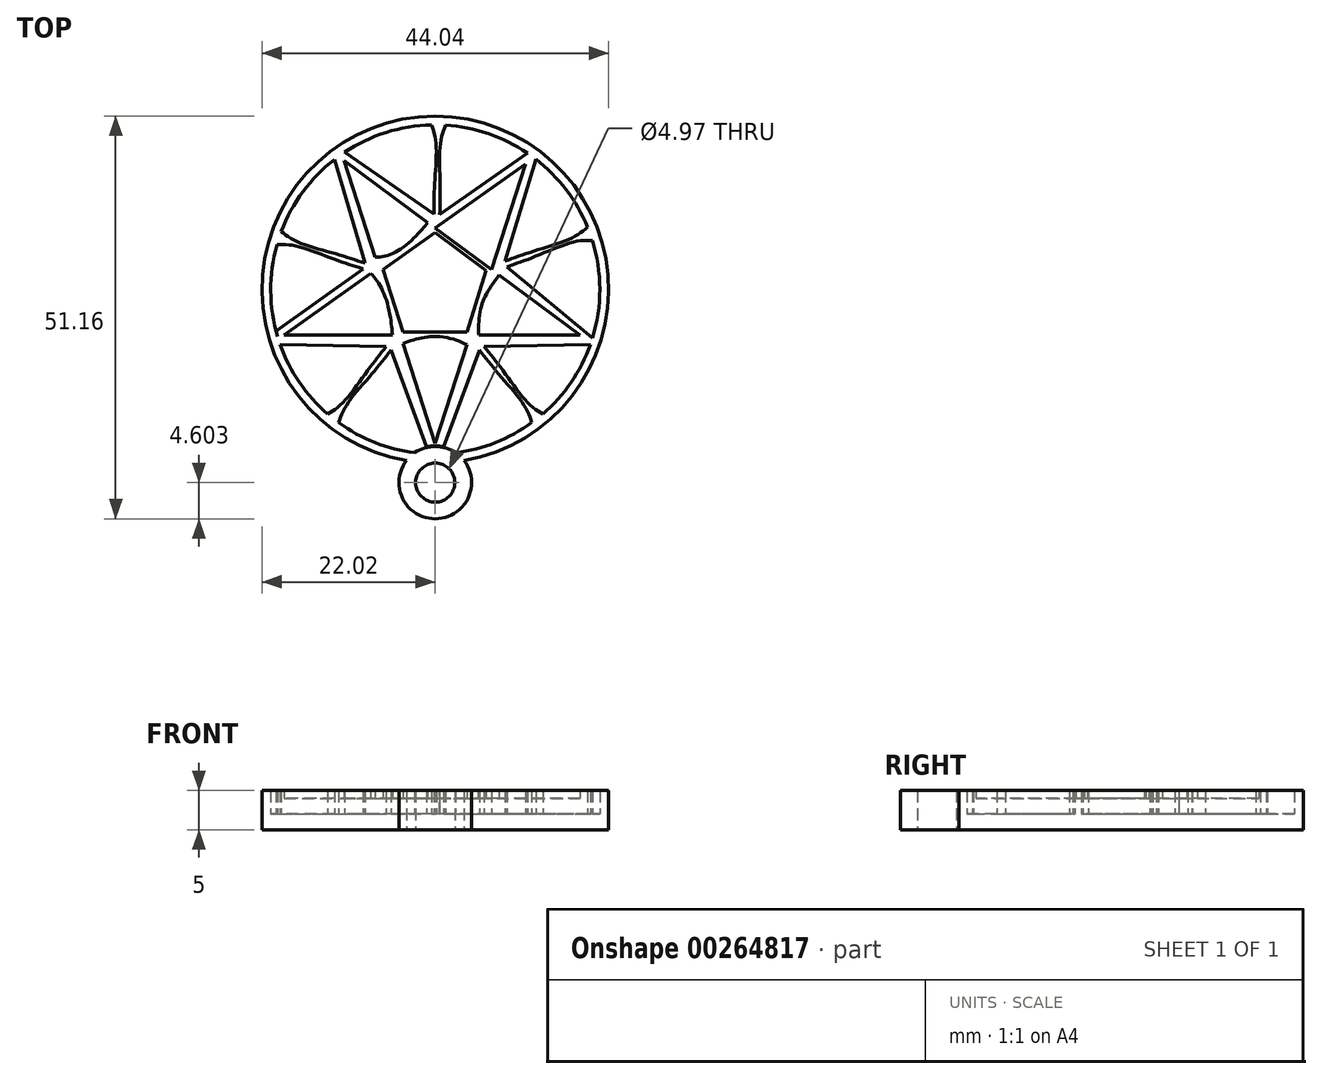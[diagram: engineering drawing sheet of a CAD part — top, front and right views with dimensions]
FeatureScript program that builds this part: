
annotation { "Feature Type Name" : "Feature", "Feature Type Description" : "" }
export const myFeature = defineFeature(function(context is Context, id is Id, definition is map)
    precondition{}
    {
        {
            var Q0;
            Q0=qCreatedBy(makeId("Top.planeOp"),FACE);
            var sketch = newSketch(context, id + "F0", { "sketchPlane" : qUnion([Q0])});
            skCircle(sketch, "E0", {"center": v(0, 0) * mm, "radius": 22.02 * mm});
            skLineSegment(sketch, "E1", {"start": v(0, 0) * mm, "end": v(0, 22.02) * mm, "construction": true});
            skLineSegment(sketch, "E2", {"start": v(0, 0) * mm, "end": v(20.72, 7.45) * mm, "construction": true});
            skLineSegment(sketch, "E3", {"start": v(0, 0) * mm, "end": v(13.06, -17.72) * mm, "construction": true});
            skLineSegment(sketch, "E4", {"start": v(0, 0) * mm, "end": v(-13.06, -17.72) * mm, "construction": true});
            skLineSegment(sketch, "E5", {"start": v(0, 0) * mm, "end": v(-20.91, 6.88) * mm, "construction": true});
            skLineSegment(sketch, "E6", {"start": v(-13.06, 17.72) * mm, "end": v(0, -22.02) * mm, "construction": true});
            skLineSegment(sketch, "E7", {"start": v(0, -22.02) * mm, "end": v(13.06, 17.72) * mm, "construction": true});
            skLineSegment(sketch, "E8", {"start": v(13.06, 17.72) * mm, "end": v(-20.91, -6.88) * mm, "construction": true});
            skLineSegment(sketch, "E9", {"start": v(-20.91, -6.88) * mm, "end": v(20.72, -6.88) * mm, "construction": true});
            skLineSegment(sketch, "E10", {"start": v(20.72, -6.88) * mm, "end": v(-13.06, 17.72) * mm, "construction": true});
            skCircle(sketch, "E11", {"center": v(0, 0) * mm, "radius": 20.9 * mm});
            skLineSegment(sketch, "E12", {"start": v(-11.47, 15.95) * mm, "end": v(0, -18.94) * mm});
            skLineSegment(sketch, "E13", {"start": v(0, -18.94) * mm, "end": v(11.36, 15.61) * mm});
            skLineSegment(sketch, "E14", {"start": v(11.36, 15.61) * mm, "end": v(-18.96, -5.83) * mm});
            skLineSegment(sketch, "E15", {"start": v(-18.96, -5.83) * mm, "end": v(18.12, -5.83) * mm});
            skLineSegment(sketch, "E16", {"start": v(18.12, -5.83) * mm, "end": v(-11.47, 15.95) * mm});
            skSolve(sketch);
        }
        {
            var Q0;
            Q0=makeQuery(id+"F0.imprint","IMPRINT",FACE,{"disambiguationData":[TD([[makeQuery(id+"F0.imprint","IMPRINT",EDGE,{"derivedFrom":sQuery(id+"F0.wireOp",EDGE,"E11")}),1.0]])]});
            var Q1;
            {var subQ0=sQuery(id+"F0.wireOp",EDGE,"E14");var subQ1=sQuery(id+"F0.wireOp",EDGE,"E13");var subQ2=makeQuery(id+"F0.imprint","INTERSECT",VERTEX,{"derivedFrom":[subQ1,subQ0]});Q1=makeQuery(id+"F0.imprint","IMPRINT",FACE,{"disambiguationData":[TD([[makeQuery(id+"F0.imprint","IMPRINT",EDGE,{"disambiguationData":[TD([[subQ2,1.0]])],"derivedFrom":subQ1}),1.0]])]});}
            var Q2;
            {var subQ0=sQuery(id+"F0.wireOp",EDGE,"E16");var subQ1=sQuery(id+"F0.wireOp",EDGE,"E12");var subQ2=makeQuery(id+"F0.imprint","INTERSECT",VERTEX,{"derivedFrom":[subQ1,subQ0]});Q2=makeQuery(id+"F0.imprint","IMPRINT",FACE,{"disambiguationData":[TD([[makeQuery(id+"F0.imprint","IMPRINT",EDGE,{"disambiguationData":[TD([[subQ2,-1.0]])],"derivedFrom":subQ1}),1.0]])]});}
            var Q3;
            {var subQ0=sQuery(id+"F0.wireOp",EDGE,"E14");var subQ1=sQuery(id+"F0.wireOp",EDGE,"E12");var subQ2=makeQuery(id+"F0.imprint","INTERSECT",VERTEX,{"derivedFrom":[subQ1,subQ0]});Q3=makeQuery(id+"F0.imprint","IMPRINT",FACE,{"disambiguationData":[TD([[makeQuery(id+"F0.imprint","IMPRINT",EDGE,{"disambiguationData":[TD([[subQ2,-1.0]])],"derivedFrom":subQ1}),-1.0]])]});}
            var Q4;
            {var subQ0=sQuery(id+"F0.wireOp",EDGE,"E13");var subQ1=sQuery(id+"F0.wireOp",EDGE,"E12");var subQ2=makeQuery(id+"F0.imprint","INTERSECT",VERTEX,{"derivedFrom":[subQ1,subQ0]});Q4=makeQuery(id+"F0.imprint","IMPRINT",FACE,{"disambiguationData":[TD([[makeQuery(id+"F0.imprint","IMPRINT",EDGE,{"disambiguationData":[TD([[subQ2,1.0]])],"derivedFrom":subQ1}),1.0]])]});}
            var Q5;
            {var subQ0=sQuery(id+"F0.wireOp",EDGE,"E15");var subQ1=sQuery(id+"F0.wireOp",EDGE,"E13");var subQ2=makeQuery(id+"F0.imprint","INTERSECT",VERTEX,{"derivedFrom":[subQ1,subQ0]});Q5=makeQuery(id+"F0.imprint","IMPRINT",FACE,{"disambiguationData":[TD([[makeQuery(id+"F0.imprint","IMPRINT",EDGE,{"disambiguationData":[TD([[subQ2,-1.0]])],"derivedFrom":subQ1}),-1.0]])]});}
            var Q6;
            {var subQ1=sQuery(id+"F0.wireOp",EDGE,"E12");var subQ5=sQuery(id+"F0.wireOp",EDGE,"E14");var subQ6=makeQuery(id+"F0.imprint","INTERSECT",VERTEX,{"derivedFrom":[subQ1,subQ5]});Q6=makeQuery(id+"F0.imprint","IMPRINT",FACE,{"disambiguationData":[TD([[makeQuery(id+"F0.imprint","IMPRINT",EDGE,{"disambiguationData":[TD([[subQ6,-1.0]])],"derivedFrom":subQ1}),1.0]])]});}
            extrude(context, id + "F1", {"entities" : qUnion([Q0, Q1, Q2, Q3, Q4, Q5, Q6]), "depth" : 2 * mm, "offsetDistance" : 25 * mm});
        }
        {
            var Q0;
            Q0=makeQuery(id+"F0.imprint","IMPRINT",FACE,{"disambiguationData":[TD([[makeQuery(id+"F0.imprint","IMPRINT",EDGE,{"derivedFrom":sQuery(id+"F0.wireOp",EDGE,"E0")}),1.0]])]});
            extrude(context, id + "F2", {"entities" : qUnion([Q0]), "operationType" : NewBodyOperationType.ADD, "depth" : 5 * mm, "offsetDistance" : 25 * mm});
        }
        {
            var Q0;
            Q0=makeQuery(id+"F1.opExtrude","CAP_FACE",FACE,{"disambiguationData":[OSD([sQuery(id+"F0.wireOp",EDGE,"E11")])],"isStart":false});
            var sketch = newSketch(context, id + "F3", { "sketchPlane" : qUnion([Q0])});
            skLineSegment(sketch, "E17", {"start": v(-11.59, 16.36) * mm, "end": v(0, -19.6) * mm});
            skLineSegment(sketch, "E18", {"start": v(0, -19.6) * mm, "end": v(11.46, 15.95) * mm});
            skLineSegment(sketch, "E19", {"start": v(11.46, 15.95) * mm, "end": v(-19.22, -5.77) * mm});
            skLineSegment(sketch, "E20", {"start": v(-19.22, -5.77) * mm, "end": v(18.4, -5.77) * mm});
            skLineSegment(sketch, "E21", {"start": v(18.4, -5.77) * mm, "end": v(-11.59, 16.36) * mm});
            skPoint(sketch, "E22.2.internal.snap0", {"position": v(-3.88, 5.1) * mm});
            skFitSpline(sketch, "E22", {"points": [v(-7.63, 4.09) * mm, v(-6, 4.35) * mm, v(-3.88, 5.51) * mm, v(-1.86, 7.4) * mm, v(-0.97, 8.52) * mm], "startDerivative": vector(7.1, 0.61) * mm, "endDerivative": vector(3.7, 5) * mm});
            skFitSpline(sketch, "E23.MirrorCS", {"points": [v(7.63, 4.09) * mm, v(6, 4.35) * mm, v(3.88, 5.51) * mm, v(1.86, 7.4) * mm, v(0.97, 8.52) * mm], "startDerivative": vector(-7.1, 0.61) * mm, "endDerivative": vector(-3.7, 5) * mm});
            skFitSpline(sketch, "E24", {"points": [v(0.97, 8.52) * mm, v(1.86, 7.4) * mm, v(3.88, 5.51) * mm, v(6, 4.35) * mm, v(7.63, 4.09) * mm], "startDerivative": vector(3.71, -5.02) * mm, "endDerivative": vector(7.1, -0.61) * mm});
            skFitSpline(sketch, "E25", {"points": [v(-8.2, 2.03) * mm, v(-7.19, 0.78) * mm, v(-6.13, -1.62) * mm, v(-5.57, -4.53) * mm, v(-5.44, -5.77) * mm], "startDerivative": vector(4.84, -5) * mm, "endDerivative": vector(0.3, -5.7) * mm});
            skPoint(sketch, "E26", {"position": v(-5.8, -1.62) * mm});
            skFitSpline(sketch, "E27", {"points": [v(-4.1, -6.89) * mm, v(-2.2, -6.27) * mm, v(0, -5.98) * mm, v(2.75, -6.44) * mm, v(4.05, -7.03) * mm], "startDerivative": vector(7.54, 3.7) * mm, "endDerivative": vector(5.89, -2.67) * mm});
            skFitSpline(sketch, "E28", {"points": [v(8.1, 1.83) * mm, v(6.5, -0.54) * mm, v(5.83, -2.25) * mm, v(5.5, -4.78) * mm, v(5.54, -5.77) * mm], "startDerivative": vector(-5.96, -8.34) * mm, "endDerivative": vector(0.52, -4.8) * mm});
            skFitSpline(sketch, "E29", {"points": [v(-20.36, 5.66) * mm, v(-17.82, 5.55) * mm, v(-12.86, 3.85) * mm, v(-9.19, 2.62) * mm], "startDerivative": vector(8.48, 0.55) * mm, "endDerivative": vector(10.23, -3.2) * mm});
            skFitSpline(sketch, "E30.MirrorCS", {"points": [v(-19.75, 7.53) * mm, v(-17.64, 6.1) * mm, v(-12.63, 4.53) * mm, v(-8.95, 3.34) * mm], "startDerivative": vector(6.5, -5.47) * mm, "endDerivative": vector(10.13, -3.49) * mm});
            skLineSegment(sketch, "E31", {"start": v(-19.22, -5.77) * mm, "end": v(0, 0) * mm, "construction": true});
            skLineSegment(sketch, "E32", {"start": v(0, 0) * mm, "end": v(11.46, 15.95) * mm, "construction": true});
            skLineSegment(sketch, "E33", {"start": v(-11.59, 16.36) * mm, "end": v(-10.84, 15.8) * mm, "construction": true});
            skLineSegment(sketch, "E34", {"start": v(-11.59, 16.36) * mm, "end": v(0, 0) * mm, "construction": true});
            skLineSegment(sketch, "E35", {"start": v(0, -0.7) * mm, "end": v(0, 0) * mm, "construction": true});
            skFitSpline(sketch, "E36.MirrorCS", {"points": [v(-13.87, -15.94) * mm, v(-11.8, -14.46) * mm, v(-8.6, -10.3) * mm, v(-6.22, -7.25) * mm], "startDerivative": vector(7.38, 4.21) * mm, "endDerivative": vector(6.77, 8.3) * mm});
            skFitSpline(sketch, "E37.MirrorCS", {"points": [v(-12.33, -17.17) * mm, v(-11.35, -14.82) * mm, v(-8.05, -10.74) * mm, v(-5.62, -7.72) * mm], "startDerivative": vector(2.4, 8.15) * mm, "endDerivative": vector(6.53, 8.5) * mm});
            skFitSpline(sketch, "E38.MirrorCS", {"points": [v(1.41, 21.09) * mm, v(0.67, 18.65) * mm, v(0.63, 13.4) * mm, v(0.57, 9.54) * mm], "startDerivative": vector(-3.33, -7.82) * mm, "endDerivative": vector(-0.37, -10.7) * mm});
            skFitSpline(sketch, "E39.MirrorCS", {"points": [v(-0.56, 21.13) * mm, v(0.09, 18.67) * mm, v(-0.08, 13.42) * mm, v(-0.19, 9.55) * mm], "startDerivative": vector(3, -7.94) * mm, "endDerivative": vector(-0.07, -10.72) * mm});
            skFitSpline(sketch, "E40.MirrorCS", {"points": [v(19.53, 8.08) * mm, v(17.46, 6.6) * mm, v(12.5, 4.88) * mm, v(8.85, 3.59) * mm], "startDerivative": vector(-6.34, -5.65) * mm, "endDerivative": vector(-10.03, -3.77) * mm});
            skFitSpline(sketch, "E41.MirrorCS", {"points": [v(20.2, 6.22) * mm, v(17.66, 6.05) * mm, v(12.74, 4.2) * mm, v(9.1, 2.87) * mm], "startDerivative": vector(-8.49, 0.31) * mm, "endDerivative": vector(-10.13, -3.49) * mm});
            skFitSpline(sketch, "E42.MirrorCS", {"points": [v(12.33, -17.17) * mm, v(11.35, -14.82) * mm, v(8.05, -10.74) * mm, v(5.62, -7.72) * mm], "startDerivative": vector(-2.4, 8.15) * mm, "endDerivative": vector(-6.53, 8.5) * mm});
            skFitSpline(sketch, "E43.MirrorCS", {"points": [v(13.87, -15.94) * mm, v(11.8, -14.46) * mm, v(8.6, -10.3) * mm, v(6.22, -7.25) * mm], "startDerivative": vector(-7.38, 4.21) * mm, "endDerivative": vector(-6.77, 8.3) * mm});
            skLineSegment(sketch, "E44", {"start": v(0, 0) * mm, "end": v(18.4, -5.77) * mm, "construction": true});
            skLineSegment(sketch, "E45", {"start": v(-19.76, -7) * mm, "end": v(-6.22, -7.25) * mm});
            skLineSegment(sketch, "E46", {"start": v(-19.76, -7) * mm, "end": v(-20.22, -5.27) * mm});
            skLineSegment(sketch, "E47", {"start": v(-20.22, -5.27) * mm, "end": v(-9.19, 2.62) * mm});
            skLineSegment(sketch, "E48", {"start": v(-19.75, 7.53) * mm, "end": v(-20.36, 5.66) * mm});
            skLineSegment(sketch, "E49", {"start": v(-13.87, -15.94) * mm, "end": v(-12.33, -17.17) * mm});
            skLineSegment(sketch, "E50", {"start": v(-5.62, -7.72) * mm, "end": v(-0.76, -20.96) * mm});
            skLineSegment(sketch, "E51", {"start": v(-0.76, -20.96) * mm, "end": v(0.71, -20.99) * mm});
            skLineSegment(sketch, "E52", {"start": v(0.71, -20.99) * mm, "end": v(5.62, -7.72) * mm});
            skLineSegment(sketch, "E53", {"start": v(12.33, -17.17) * mm, "end": v(13.87, -15.94) * mm});
            skLineSegment(sketch, "E54", {"start": v(6.22, -7.25) * mm, "end": v(19.85, -7) * mm});
            skLineSegment(sketch, "E55", {"start": v(19.85, -7) * mm, "end": v(20.08, -6.26) * mm});
            skLineSegment(sketch, "E56", {"start": v(9.1, 2.87) * mm, "end": v(20.08, -6.26) * mm});
            skLineSegment(sketch, "E57", {"start": v(19.53, 8.08) * mm, "end": v(20.2, 6.22) * mm});
            skLineSegment(sketch, "E58", {"start": v(8.85, 3.59) * mm, "end": v(12.8, 16.66) * mm});
            skLineSegment(sketch, "E59", {"start": v(12.8, 16.66) * mm, "end": v(11.8, 17.4) * mm});
            skLineSegment(sketch, "E60", {"start": v(11.8, 17.4) * mm, "end": v(0.57, 9.54) * mm});
            skLineSegment(sketch, "E61", {"start": v(1.41, 21.09) * mm, "end": v(-0.56, 21.13) * mm});
            skLineSegment(sketch, "E62", {"start": v(-0.19, 9.55) * mm, "end": v(-11.66, 17.51) * mm});
            skLineSegment(sketch, "E63", {"start": v(-11.66, 17.51) * mm, "end": v(-12.84, 16.68) * mm});
            skLineSegment(sketch, "E64", {"start": v(-12.84, 16.68) * mm, "end": v(-8.95, 3.34) * mm});
            skLineSegment(sketch, "E65", {"start": v(-6.63, 2.52) * mm, "end": v(-4.07, -5.4) * mm});
            skLineSegment(sketch, "E66", {"start": v(-4.07, -5.4) * mm, "end": v(4.07, -5.4) * mm});
            skLineSegment(sketch, "E67", {"start": v(4.07, -5.4) * mm, "end": v(6.47, 2.38) * mm});
            skLineSegment(sketch, "E68", {"start": v(6.47, 2.38) * mm, "end": v(0, 7.22) * mm});
            skLineSegment(sketch, "E69", {"start": v(0, 7.22) * mm, "end": v(-6.63, 2.52) * mm});
            skCircle(sketch, "E70", {"center": v(0, -24.64) * mm, "radius": 4.75 * mm});
            skCircle(sketch, "E71", {"center": v(0, -24.64) * mm, "radius": 2.5 * mm});
            skLineSegment(sketch, "E72", {"start": v(2.5, -24.53) * mm, "end": v(-2.5, -24.64) * mm, "construction": true});
            skSolve(sketch);
        }
        {
            var Q0;
            {var subQ3=sQuery(id+"F3.wireOp",EDGE,"E22");Q0=makeQuery(id+"F3.imprint","IMPRINT",FACE,{"disambiguationData":[TD([[makeQuery(id+"F3.imprint","IMPRINT",EDGE,{"derivedFrom":subQ3}),1.0]])]});}
            var Q1;
            {var subQ3=sQuery(id+"F3.wireOp",EDGE,"E24");var subQ6=makeQuery(id+"F3.imprint","IMPRINT",VERTEX,{"derivedFrom":subQ3});Q1=makeQuery(id+"F3.imprint","IMPRINT",FACE,{"disambiguationData":[TD([[makeQuery(id+"F3.imprint","IMPRINT",EDGE,{"disambiguationData":[TD([[subQ6,1.0]])],"derivedFrom":subQ3}),1.0]])]});}
            var Q2;
            {var subQ3=sQuery(id+"F3.wireOp",EDGE,"E25");Q2=makeQuery(id+"F3.imprint","IMPRINT",FACE,{"disambiguationData":[TD([[makeQuery(id+"F3.imprint","IMPRINT",EDGE,{"derivedFrom":subQ3}),-1.0]])]});}
            var Q3;
            {var subQ3=sQuery(id+"F3.wireOp",EDGE,"E27");Q3=makeQuery(id+"F3.imprint","IMPRINT",FACE,{"disambiguationData":[TD([[makeQuery(id+"F3.imprint","IMPRINT",EDGE,{"derivedFrom":subQ3}),-1.0]])]});}
            var Q4;
            {var subQ3=sQuery(id+"F3.wireOp",EDGE,"E28");Q4=makeQuery(id+"F3.imprint","IMPRINT",FACE,{"disambiguationData":[TD([[makeQuery(id+"F3.imprint","IMPRINT",EDGE,{"derivedFrom":subQ3}),1.0]])]});}
            var Q5;
            Q5=makeQuery(id+"F3.imprint","IMPRINT",FACE,{"disambiguationData":[TD([[makeQuery(id+"F3.imprint","IMPRINT",EDGE,{"derivedFrom":sQuery(id+"F3.wireOp",EDGE,"E65")}),1.0]])]});
            extrude(context, id + "F4", {"entities" : qUnion([Q0, Q1, Q2, Q3, Q4, Q5]), "operationType" : NewBodyOperationType.ADD, "depth" : 2 * mm, "offsetDistance" : 25 * mm});
        }
        {
            var Q0;
            Q0=makeQuery(id+"F3.imprint","IMPRINT",FACE,{"disambiguationData":[TD([[makeQuery(id+"F3.imprint","IMPRINT",EDGE,{"derivedFrom":sQuery(id+"F3.wireOp",EDGE,"E29")}),1.0]])]});
            var Q1;
            {var subQ5=sQuery(id+"F3.wireOp",EDGE,"E25");Q1=makeQuery(id+"F3.imprint","IMPRINT",FACE,{"disambiguationData":[TD([[makeQuery(id+"F3.imprint","IMPRINT",EDGE,{"derivedFrom":subQ5}),1.0]])]});}
            var Q2;
            {var subQ0=sQuery(id+"F3.wireOp",EDGE,"E22");Q2=makeQuery(id+"F3.imprint","IMPRINT",FACE,{"disambiguationData":[TD([[makeQuery(id+"F3.imprint","IMPRINT",EDGE,{"derivedFrom":subQ0}),-1.0]])]});}
            var Q3;
            {var subQ5=sQuery(id+"F3.wireOp",EDGE,"E24");var subQ7=makeQuery(id+"F3.imprint","IMPRINT",VERTEX,{"derivedFrom":subQ5});Q3=makeQuery(id+"F3.imprint","IMPRINT",FACE,{"disambiguationData":[TD([[makeQuery(id+"F3.imprint","IMPRINT",EDGE,{"disambiguationData":[TD([[subQ7,1.0]])],"derivedFrom":subQ5}),-1.0]])]});}
            var Q4;
            {var subQ5=sQuery(id+"F3.wireOp",EDGE,"E28");Q4=makeQuery(id+"F3.imprint","IMPRINT",FACE,{"disambiguationData":[TD([[makeQuery(id+"F3.imprint","IMPRINT",EDGE,{"derivedFrom":subQ5}),-1.0]])]});}
            var Q5;
            Q5=makeQuery(id+"F3.imprint","IMPRINT",FACE,{"disambiguationData":[TD([[makeQuery(id+"F3.imprint","IMPRINT",EDGE,{"derivedFrom":sQuery(id+"F3.wireOp",EDGE,"E65")}),-1.0]])]});
            var Q6;
            {var subQ0=sQuery(id+"F3.wireOp",EDGE,"E27");Q6=makeQuery(id+"F3.imprint","IMPRINT",FACE,{"disambiguationData":[TD([[makeQuery(id+"F3.imprint","IMPRINT",EDGE,{"derivedFrom":subQ0}),1.0]])]});}
            var Q7;
            {var subQ33=sQuery(id+"F3.wireOp",EDGE,"E47");Q7=makeQuery(id+"F3.imprint","IMPRINT",FACE,{"disambiguationData":[TD([[makeQuery(id+"F3.imprint","IMPRINT",EDGE,{"derivedFrom":subQ33}),-1.0]])]});}
            extrude(context, id + "F5", {"entities" : qUnion([Q0, Q1, Q2, Q3, Q4, Q5, Q6, Q7]), "operationType" : NewBodyOperationType.ADD, "depth" : 3 * mm, "offsetDistance" : 25 * mm});
        }
        {
            var Q0;
            Q0=qCreatedBy(makeId("Top.planeOp"),FACE);
            var sketch = newSketch(context, id + "F6", { "sketchPlane" : qUnion([Q0])});
            skCircle(sketch, "E73", {"center": v(0, -24.54) * mm, "radius": 4.6 * mm});
            skCircle(sketch, "E74", {"center": v(0, -24.54) * mm, "radius": 2.49 * mm});
            skSolve(sketch);
        }
        {
            var Q0;
            Q0=makeQuery(id+"F6.imprint","IMPRINT",FACE,{"disambiguationData":[TD([[makeQuery(id+"F6.imprint","IMPRINT",EDGE,{"derivedFrom":sQuery(id+"F6.wireOp",EDGE,"E73")}),1.0]])]});
            extrude(context, id + "F7", {"entities" : qUnion([Q0]), "operationType" : NewBodyOperationType.ADD, "depth" : 5 * mm, "offsetDistance" : 25 * mm});
        }
    });
